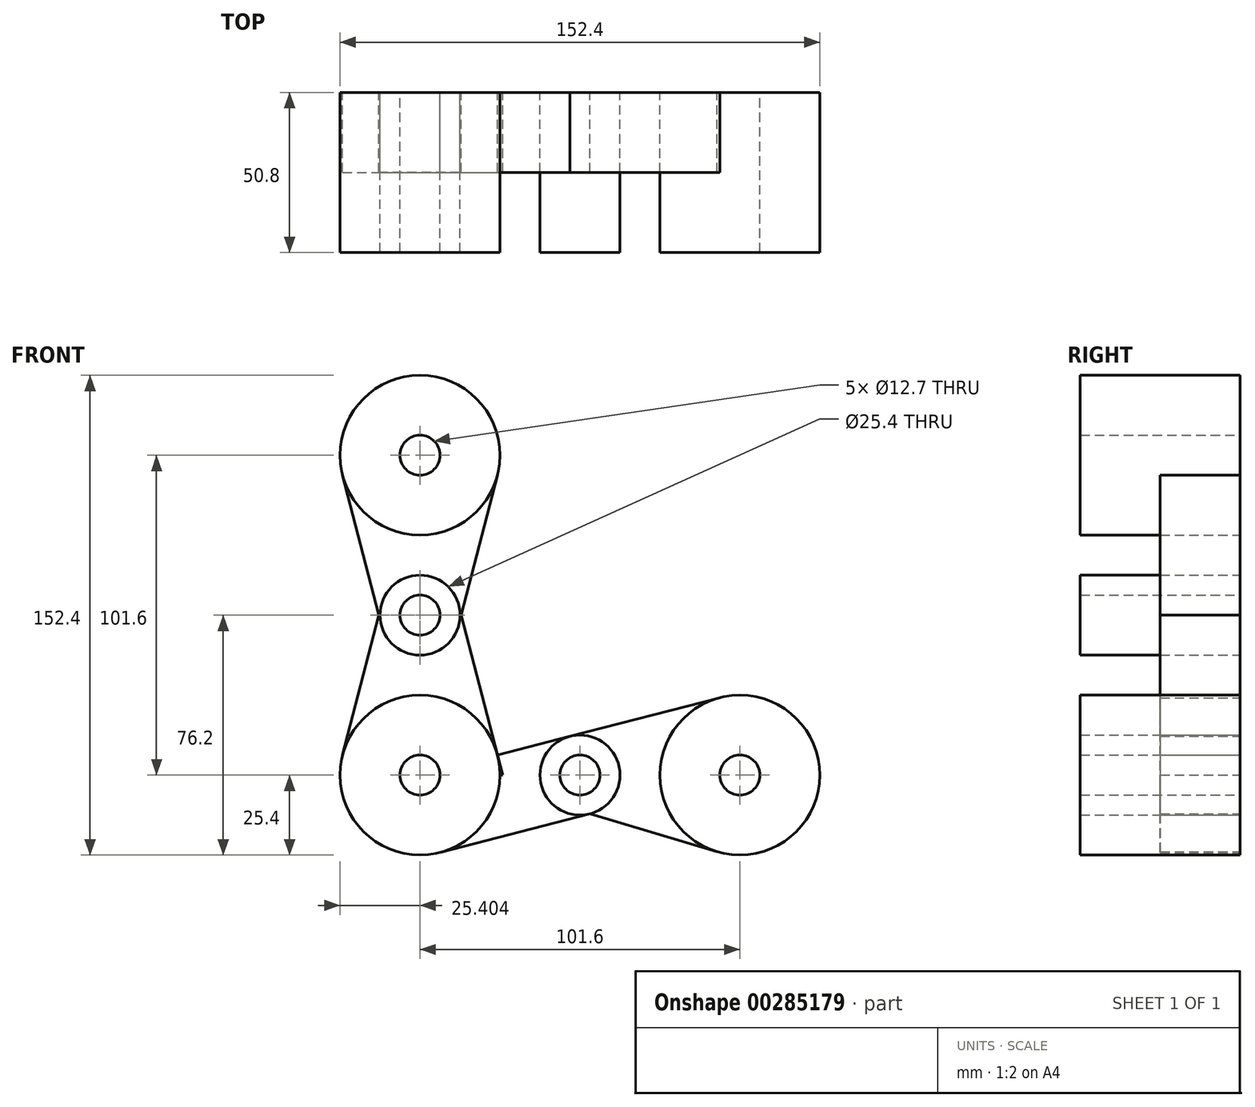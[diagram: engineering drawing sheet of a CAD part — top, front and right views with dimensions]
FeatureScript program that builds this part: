
annotation { "Feature Type Name" : "Feature", "Feature Type Description" : "" }
export const myFeature = defineFeature(function(context is Context, id is Id, definition is map)
    precondition{}
    {
        {
            var Q0;
            Q0=qCreatedBy(makeId("Front.planeOp"),FACE);
            var sketch = newSketch(context, id + "F0", { "sketchPlane" : qUnion([Q0])});
            skLineSegment(sketch, "E0", {"start": v(-100.5, -50.8) * mm, "end": v(-49.7, -50.8) * mm});
            skLineSegment(sketch, "E1", {"start": v(-49.7, -50.8) * mm, "end": v(1.1, -50.8) * mm});
            skLineSegment(sketch, "E2", {"start": v(-100.5, -50.8) * mm, "end": v(-100.5, 0) * mm});
            skLineSegment(sketch, "E3", {"start": v(-100.5, 0) * mm, "end": v(-100.5, 50.8) * mm});
            skCircle(sketch, "E4", {"center": v(-100.5, 50.8) * mm, "radius": 25.4 * mm});
            skCircle(sketch, "E5", {"center": v(-100.5, -50.8) * mm, "radius": 25.4 * mm});
            skCircle(sketch, "E6", {"center": v(1.1, -50.8) * mm, "radius": 25.4 * mm});
            skCircle(sketch, "E7", {"center": v(-100.5, 0) * mm, "radius": 12.7 * mm});
            skCircle(sketch, "E8", {"center": v(-49.7, -50.8) * mm, "radius": 12.7 * mm});
            skLineSegment(sketch, "E9", {"start": v(-126.75, 50.87) * mm, "end": v(-113.61, 0) * mm});
            skLineSegment(sketch, "E10", {"start": v(-113.61, 0) * mm, "end": v(-125.09, -44.45) * mm});
            skLineSegment(sketch, "E11", {"start": v(-75.9, 44.45) * mm, "end": v(-87.38, 0) * mm});
            skLineSegment(sketch, "E12", {"start": v(-87.38, 0) * mm, "end": v(-74.26, -50.8) * mm});
            skLineSegment(sketch, "E13", {"start": v(-52.87, -38.5) * mm, "end": v(0, -24.85) * mm});
            skLineSegment(sketch, "E14", {"start": v(-94.15, -75.4) * mm, "end": v(-46.52, -63.1) * mm});
            skLineSegment(sketch, "E15", {"start": v(-46.52, -63.1) * mm, "end": v(0, -76.98) * mm});
            skLineSegment(sketch, "E16", {"start": v(-52.87, -38.5) * mm, "end": v(-75.9, -44.45) * mm});
            skSolve(sketch);
        }
        {
            var Q0;
            {var subQ0=sQuery(id+"F0.wireOp",EDGE,"E4");var subQ1=makeQuery(id+"F0.imprint","INTERSECT",VERTEX,{"derivedFrom":[subQ0,sQuery(id+"F0.wireOp",EDGE,"E9")]});Q0=makeQuery(id+"F0.imprint","IMPRINT",FACE,{"disambiguationData":[TD([[makeQuery(id+"F0.imprint","IMPRINT",EDGE,{"disambiguationData":[TD([[subQ1,-1.0]])],"derivedFrom":subQ0}),1.0]])]});}
            var Q1;
            {var subQ0=sQuery(id+"F0.wireOp",EDGE,"E3");var subQ1=sQuery(id+"F0.wireOp",EDGE,"E2");var subQ2=makeQuery(id+"F0.imprint","INTERSECT",VERTEX,{"derivedFrom":[subQ1,subQ0]});Q1=makeQuery(id+"F0.imprint","IMPRINT",FACE,{"disambiguationData":[TD([[makeQuery(id+"F0.imprint","IMPRINT",EDGE,{"disambiguationData":[TD([[subQ2,1.0]])],"derivedFrom":subQ1}),1.0]])]});}
            var Q2;
            {var subQ0=sQuery(id+"F0.wireOp",EDGE,"E3");var subQ1=sQuery(id+"F0.wireOp",EDGE,"E2");var subQ2=makeQuery(id+"F0.imprint","INTERSECT",VERTEX,{"derivedFrom":[subQ1,subQ0]});Q2=makeQuery(id+"F0.imprint","IMPRINT",FACE,{"disambiguationData":[TD([[makeQuery(id+"F0.imprint","IMPRINT",EDGE,{"disambiguationData":[TD([[subQ2,1.0]])],"derivedFrom":subQ1}),-1.0]])]});}
            var Q3;
            {var subQ0=sQuery(id+"F0.wireOp",EDGE,"E2");var subQ1=sQuery(id+"F0.wireOp",EDGE,"E0");var subQ2=makeQuery(id+"F0.imprint","INTERSECT",VERTEX,{"derivedFrom":[subQ1,subQ0]});Q3=makeQuery(id+"F0.imprint","IMPRINT",FACE,{"disambiguationData":[TD([[makeQuery(id+"F0.imprint","IMPRINT",EDGE,{"disambiguationData":[TD([[subQ2,-1.0]])],"derivedFrom":subQ1}),1.0]])]});}
            var Q4;
            {var subQ3=sQuery(id+"F0.wireOp",EDGE,"E2");var subQ4=sQuery(id+"F0.wireOp",EDGE,"E0");var subQ5=makeQuery(id+"F0.imprint","INTERSECT",VERTEX,{"derivedFrom":[subQ4,subQ3]});Q4=makeQuery(id+"F0.imprint","IMPRINT",FACE,{"disambiguationData":[TD([[makeQuery(id+"F0.imprint","IMPRINT",EDGE,{"disambiguationData":[TD([[subQ5,-1.0]])],"derivedFrom":subQ4}),-1.0]])]});}
            var Q5;
            {var subQ0=sQuery(id+"F0.wireOp",EDGE,"E1");var subQ1=sQuery(id+"F0.wireOp",EDGE,"E0");var subQ2=makeQuery(id+"F0.imprint","INTERSECT",VERTEX,{"derivedFrom":[subQ1,subQ0]});Q5=makeQuery(id+"F0.imprint","IMPRINT",FACE,{"disambiguationData":[TD([[makeQuery(id+"F0.imprint","IMPRINT",EDGE,{"disambiguationData":[TD([[subQ2,1.0]])],"derivedFrom":subQ1}),-1.0]])]});}
            var Q6;
            {var subQ0=sQuery(id+"F0.wireOp",EDGE,"E1");var subQ1=sQuery(id+"F0.wireOp",EDGE,"E0");var subQ2=makeQuery(id+"F0.imprint","INTERSECT",VERTEX,{"derivedFrom":[subQ1,subQ0]});Q6=makeQuery(id+"F0.imprint","IMPRINT",FACE,{"disambiguationData":[TD([[makeQuery(id+"F0.imprint","IMPRINT",EDGE,{"disambiguationData":[TD([[subQ2,1.0]])],"derivedFrom":subQ1}),1.0]])]});}
            var Q7;
            {var subQ0=sQuery(id+"F0.wireOp",EDGE,"E6");var subQ1=makeQuery(id+"F0.imprint","INTERSECT",VERTEX,{"derivedFrom":[subQ0,sQuery(id+"F0.wireOp",EDGE,"E13")]});Q7=makeQuery(id+"F0.imprint","IMPRINT",FACE,{"disambiguationData":[TD([[makeQuery(id+"F0.imprint","IMPRINT",EDGE,{"disambiguationData":[TD([[subQ1,-1.0]])],"derivedFrom":subQ0}),1.0]])]});}
            extrude(context, id + "F1", {"entities" : qUnion([Q0, Q1, Q2, Q3, Q4, Q5, Q6, Q7]), "depth" : 50.8 * mm});
        }
        {
            var Q0;
            {var subQ0=sQuery(id+"F0.wireOp",EDGE,"E10");Q0=makeQuery(id+"F0.imprint","IMPRINT",FACE,{"disambiguationData":[TD([[makeQuery(id+"F0.imprint","IMPRINT",EDGE,{"derivedFrom":subQ0}),1.0]])]});}
            var Q1;
            {var subQ10=sQuery(id+"F0.wireOp",EDGE,"E11");Q1=makeQuery(id+"F0.imprint","IMPRINT",FACE,{"disambiguationData":[TD([[makeQuery(id+"F0.imprint","IMPRINT",EDGE,{"derivedFrom":subQ10}),-1.0]])]});}
            var Q2;
            {var subQ0=sQuery(id+"F0.wireOp",EDGE,"E14");Q2=makeQuery(id+"F0.imprint","IMPRINT",FACE,{"disambiguationData":[TD([[makeQuery(id+"F0.imprint","IMPRINT",EDGE,{"derivedFrom":subQ0}),1.0]])]});}
            var Q3;
            {var subQ0=sQuery(id+"F0.wireOp",EDGE,"E6");var subQ1=sQuery(id+"F0.wireOp",EDGE,"E1");var subQ2=makeQuery(id+"F0.imprint","INTERSECT",VERTEX,{"derivedFrom":[subQ1,subQ0]});Q3=makeQuery(id+"F0.imprint","IMPRINT",FACE,{"disambiguationData":[TD([[makeQuery(id+"F0.imprint","IMPRINT",EDGE,{"disambiguationData":[TD([[subQ2,1.0]])],"derivedFrom":subQ1}),-1.0]])]});}
            var Q4;
            {var subQ0=sQuery(id+"F0.wireOp",EDGE,"E6");var subQ1=sQuery(id+"F0.wireOp",EDGE,"E1");var subQ2=makeQuery(id+"F0.imprint","INTERSECT",VERTEX,{"derivedFrom":[subQ1,subQ0]});Q4=makeQuery(id+"F0.imprint","IMPRINT",FACE,{"disambiguationData":[TD([[makeQuery(id+"F0.imprint","IMPRINT",EDGE,{"disambiguationData":[TD([[subQ2,1.0]])],"derivedFrom":subQ1}),1.0]])]});}
            var Q5;
            {var subQ5=sQuery(id+"F0.wireOp",EDGE,"E16");Q5=makeQuery(id+"F0.imprint","IMPRINT",FACE,{"disambiguationData":[TD([[makeQuery(id+"F0.imprint","IMPRINT",EDGE,{"derivedFrom":subQ5}),1.0]])]});}
            extrude(context, id + "F2", {"entities" : qUnion([Q0, Q1, Q2, Q3, Q4, Q5]), "depth" : 25.4 * mm});
        }
        {
            var Q0;
            Q0=sQuery(id+"F0.wireOp",VERTEX,"E4.center");
            var Q1;
            Q1=sQuery(id+"F0.wireOp",VERTEX,"E5.center");
            var Q2;
            Q2=sQuery(id+"F0.wireOp",VERTEX,"E7.center");
            var Q3;
            Q3=sQuery(id+"F0.wireOp",VERTEX,"E8.center");
            var Q4;
            Q4=sQuery(id+"F0.wireOp",VERTEX,"E1.end");
            var Q5;
            Q5=makeQuery(id+"F1.opExtrude","SWEPT_BODY",BODY,{"disambiguationData":[OSD([sQuery(id+"F0.wireOp",EDGE,"E4")])]});
            var Q6;
            Q6=makeQuery(id+"F1.opExtrude","SWEPT_BODY",BODY,{"disambiguationData":[OSD([sQuery(id+"F0.wireOp",EDGE,"E5")])]});
            var Q7;
            Q7=makeQuery(id+"F1.opExtrude","SWEPT_BODY",BODY,{"disambiguationData":[OSD([sQuery(id+"F0.wireOp",EDGE,"E7")])]});
            var Q8;
            Q8=makeQuery(id+"F1.opExtrude","SWEPT_BODY",BODY,{"disambiguationData":[OSD([sQuery(id+"F0.wireOp",EDGE,"E8")])]});
            var Q9;
            Q9=makeQuery(id+"F1.opExtrude","SWEPT_BODY",BODY,{"disambiguationData":[OSD([sQuery(id+"F0.wireOp",EDGE,"E6")])]});
            hole(context, id + "F3", {"style" : HoleStyle.SIMPLE, "endStyle" : HoleEndStyle.THROUGH, "oppositeDirection" : true, "holeDiameter" : 12.7 * mm, "tappedDepth" : 12.7 * mm, "tapClearance" : 3, "locations" : qUnion([Q0, Q1, Q2, Q3, Q4]), "scope" : qUnion([Q5, Q6, Q7, Q8, Q9])});
        }
    });
